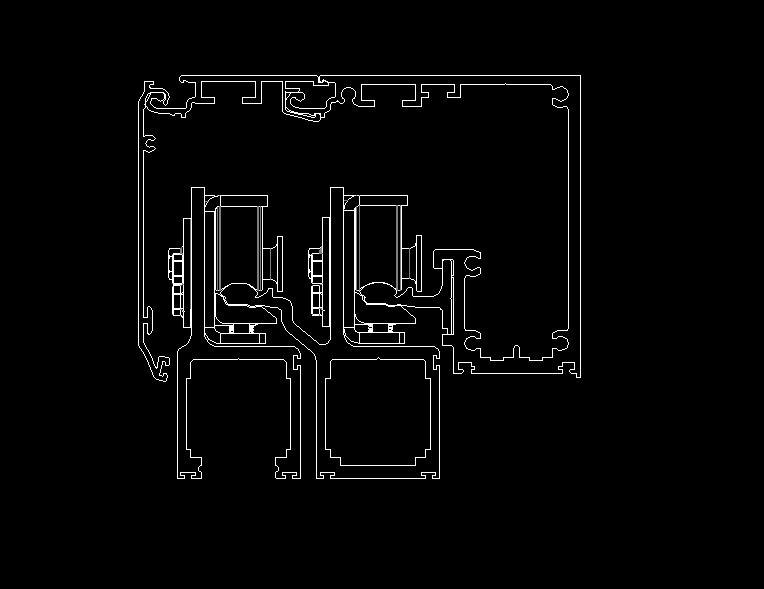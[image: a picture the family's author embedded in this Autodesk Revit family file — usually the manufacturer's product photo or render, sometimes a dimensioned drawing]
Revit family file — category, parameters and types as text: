
# Revit family: ASSA_ABLOY_TelescopicVersaMax_OHC_FBO01
name_source: partatom
category: Doors
units: mm (PartAtom-declared; Revit-internal decimal feet)

## family parameters
Always vertical = Yes
Cut with Voids When Loaded = No
Host = Wall
OmniClass Number = 23.30.10.00
OmniClass Title = Doors
Room Calculation Point = No
Shared = No

## types (3) — shared parameters
Analytic Construction = <None>
BIMobject category = Sliding Doors
Bottom Profile Height = Fix Leaf1 : 0'4''
Bottom Profile Option 01 = Fix Leaf1 : 0'4''
Bottom Profile Option 02 = Fix Leaf1 : 0'7''
Bottom Profile Option 03 = Fix Leaf1 : 0'10''
Brass Polished Finish = Brass, Polished
Brass Satin Finish = Brass, Satin
Clear Anodized = Clear Anodized
Dark Bronze Anodized = Dark Bronze Anodized
Date of publishing = 2015-02-23
Depth = 0.00
Edition number = 1
Frame Material = Clear Anodized
Function = Interior
Gap = 6 mm  [stored 0.019685 ft]
Glass = Glass
Height = 2280 mm
IFC Classification = Door
Leaf Height = 2153 mm
Manufacturer = ASSA ABLOY Entrance Systems-North America
Manufacturer name = ASSA ABLOY Entrance Systems-North America
Material main = Aluminium
NBS Reference Code = 25-30-20-77
NBS Reference Description = Sliding Doorset Systems
Nominal height = 0.00
Nominal width = 0.00
Product SKU = VersaMax_Tele_OHC
Product data url = http://besam-na.bimobject.com
Product family = ICU
Product group = Telescopic
QR code = http://besam-na.bimobject.com
Rough Height = 2286 mm  [stored 7.5 ft]
Stainless Steel Polished Finish = Stainless Steel, Polished
Stainless Steel Satin Finish = Stainless Steel, Satin
Thickness = 152 mm
Top Profile Height = 102 mm
UNSPSC Code = 301715
Uniclass 1.4 Code = L4133
Uniclass 1.4 Description = Sliding
Uniclass 2.0 Code = SS-25-30-20-77
Uniclass 2.0 Description = Sliding Doorset Systems
Wall Closure = By host
Weight Net (Kg) = 0

## per-type parameters (varying)
| type | Rough Width | Width |
| ICU-TE-3FBO-8 | 2451 mm | 2438 mm |
| ICU-TE-3FBO-10 | 3061 mm | 3048 mm  [stored 10 ft] |
| ICU-TE-3FBO-12 | 3670 mm | 3658 mm |

note: [stored X ft] marks values corroborated as IEEE doubles in the binary element streams (Revit-internal decimal feet)

## geometry (parser evidence)
native form markers: Sweep x43
no freeform markers — native parametric forms only
